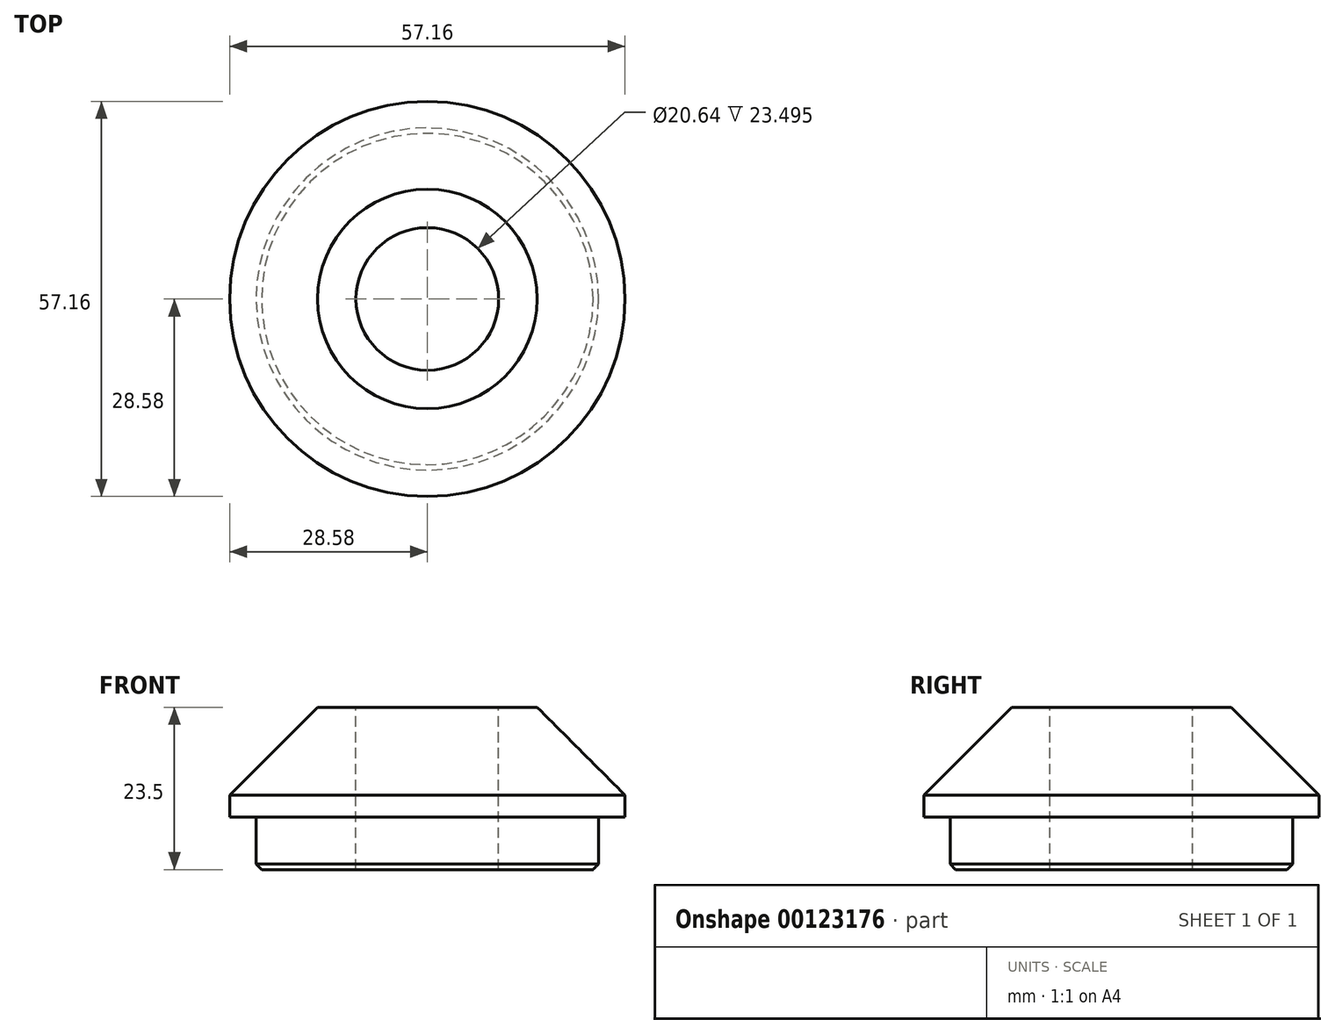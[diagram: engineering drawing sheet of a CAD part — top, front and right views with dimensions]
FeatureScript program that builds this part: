
annotation { "Feature Type Name" : "Feature", "Feature Type Description" : "" }
export const myFeature = defineFeature(function(context is Context, id is Id, definition is map)
    precondition{}
    {
        {
            var Q0;
            Q0=qCreatedBy(makeId("Top.planeOp"),FACE);
            var sketch = newSketch(context, id + "F0", { "sketchPlane" : qUnion([Q0])});
            skCircle(sketch, "E0", {"center": v(0, 0) * mm, "radius": 24.77 * mm});
            skSolve(sketch);
        }
        {
            var Q0;
            Q0 = qSketchRegion(id + "F0", true);
            extrude(context, id + "F1", {"entities" : qUnion([Q0]), "depth" : 7.62 * mm});
        }
        {
            var Q0;
            Q0=makeQuery(id+"F1.opExtrude","CAP_FACE",FACE,{"disambiguationData":[OSD([sQuery(id+"F0.wireOp",EDGE,"E0")])],"isStart":false});
            var sketch = newSketch(context, id + "F2", { "sketchPlane" : qUnion([Q0])});
            skCircle(sketch, "E1", {"center": v(0, 0) * mm, "radius": 28.58 * mm});
            skSolve(sketch);
        }
        {
            var Q0;
            Q0 = qSketchRegion(id + "F2", true);
            extrude(context, id + "F3", {"entities" : qUnion([Q0]), "operationType" : NewBodyOperationType.ADD, "depth" : 15.88 * mm});
        }
        {
            var Q0;
            Q0=makeQuery(id+"F3.opExtrude","CAP_EDGE",EDGE,{"disambiguationData":[OSD([sQuery(id+"F2.wireOp",EDGE,"E1")])],"isStart":false});
            chamfer(context, id + "F4", {"entities" : qUnion([Q0]), "chamferType" : ChamferType.OFFSET_ANGLE, "width" : 12.7 * mm, "oppositeDirection" : false, "angle" : 45 * degree, "tangentPropagation" : true});
        }
        {
            var Q0;
            Q0=makeQuery(id+"F3.opExtrude","CAP_FACE",FACE,{"disambiguationData":[OSD([sQuery(id+"F2.wireOp",EDGE,"E1")])],"isStart":false});
            var sketch = newSketch(context, id + "F5", { "sketchPlane" : qUnion([Q0])});
            skCircle(sketch, "E2", {"center": v(0, 0) * mm, "radius": 10.32 * mm});
            skSolve(sketch);
        }
        {
            var Q0;
            Q0 = qSketchRegion(id + "F5", true);
            extrude(context, id + "F6", {"entities" : qUnion([Q0]), "operationType" : NewBodyOperationType.REMOVE, "endBound" : BoundingType.THROUGH_ALL, "oppositeDirection" : true, "depth" : 25.4 * mm});
        }
        {
            var Q0;
            Q0=makeQuery(id+"F1.opExtrude","CAP_EDGE",EDGE,{"disambiguationData":[OSD([sQuery(id+"F0.wireOp",EDGE,"E0")])],"isStart":true});
            chamfer(context, id + "F7", {"entities" : qUnion([Q0]), "width" : 0.8 * mm, "tangentPropagation" : true});
        }
    });
